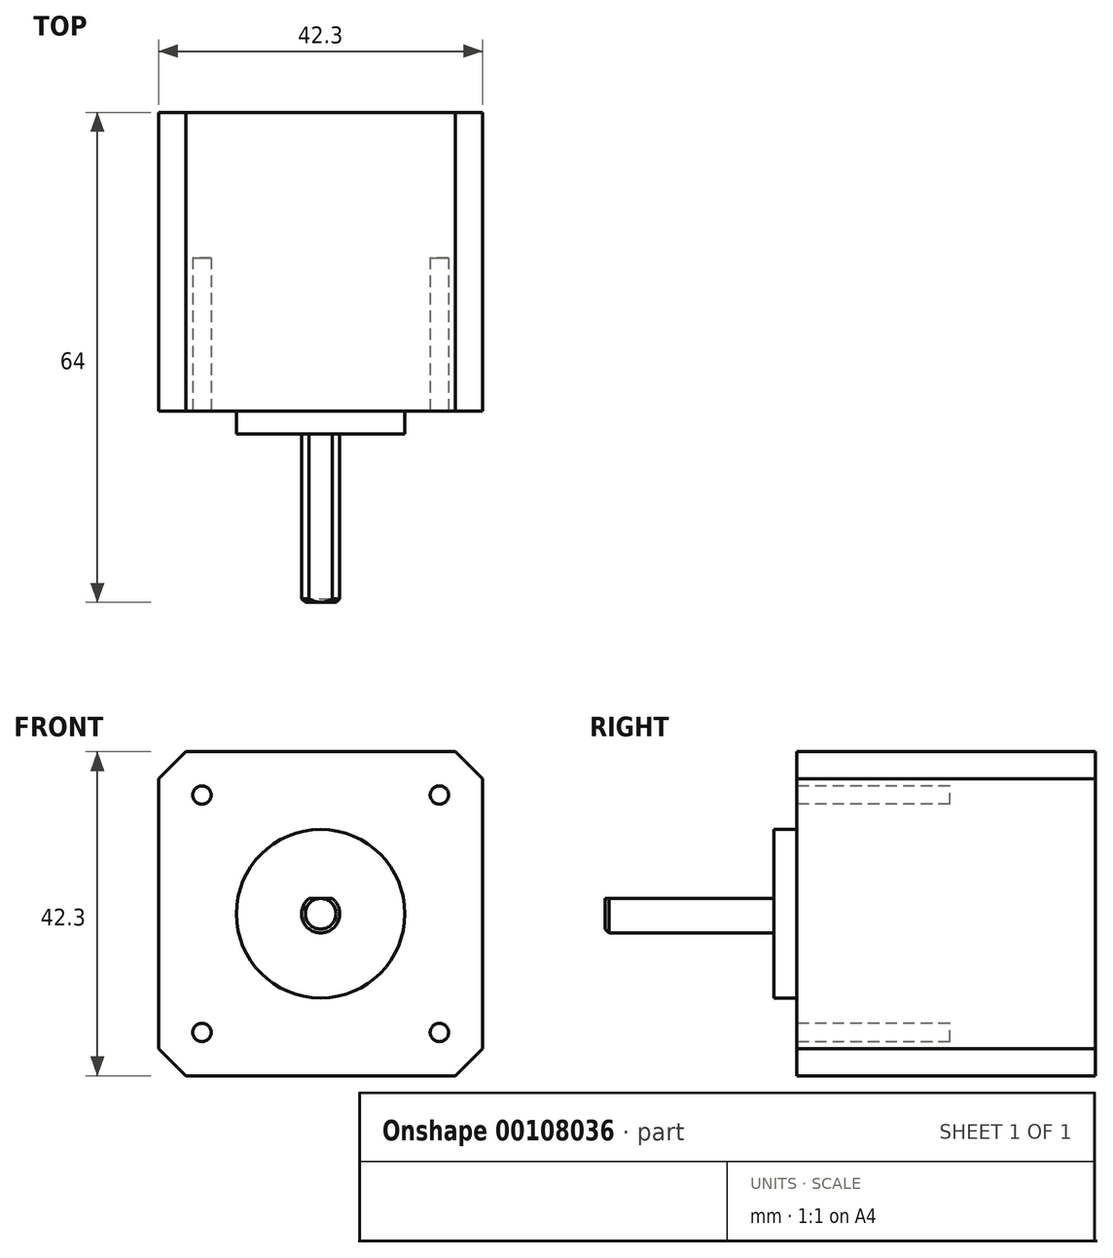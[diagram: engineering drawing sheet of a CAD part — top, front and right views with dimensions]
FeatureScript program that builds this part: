
annotation { "Feature Type Name" : "Feature", "Feature Type Description" : "" }
export const myFeature = defineFeature(function(context is Context, id is Id, definition is map)
    precondition{}
    {
        {
            var Q0;
            Q0=qCreatedBy(makeId("Front.planeOp"),FACE);
            var sketch = newSketch(context, id + "F0", { "sketchPlane" : qUnion([Q0])});
            skLineSegment(sketch, "E0.bottom", {"start": v(-17.61, 21.15) * mm, "end": v(17.61, 21.15) * mm});
            skLineSegment(sketch, "E0.top", {"start": v(-17.61, -21.15) * mm, "end": v(17.61, -21.15) * mm});
            skLineSegment(sketch, "E0.left", {"start": v(-21.15, 17.61) * mm, "end": v(-21.15, -17.61) * mm});
            skLineSegment(sketch, "E0.right", {"start": v(21.15, 17.61) * mm, "end": v(21.15, -17.61) * mm});
            skPoint(sketch, "E0.middle", {"position": v(0, 0) * mm});
            skLineSegment(sketch, "E1", {"start": v(-21.15, 17.61) * mm, "end": v(-17.61, 21.15) * mm});
            skLineSegment(sketch, "E2", {"start": v(0, 0) * mm, "end": v(0, 21.15) * mm, "construction": true});
            skLineSegment(sketch, "E3", {"start": v(0, 0) * mm, "end": v(21.15, 0) * mm, "construction": true});
            skLineSegment(sketch, "E4.MirrorCS", {"start": v(21.15, 17.61) * mm, "end": v(17.61, 21.15) * mm});
            skLineSegment(sketch, "E5.MirrorCS", {"start": v(-21.15, -17.61) * mm, "end": v(-17.61, -21.15) * mm});
            skLineSegment(sketch, "E6.MirrorCS", {"start": v(21.15, -17.61) * mm, "end": v(17.61, -21.15) * mm});
            skSolve(sketch);
        }
        {
            var Q0;
            Q0 = qSketchRegion(id + "F0", true);
            extrude(context, id + "F1", {"entities" : qUnion([Q0]), "endBound" : BoundingType.SYMMETRIC, "depth" : 39 * mm});
        }
        {
            var Q0;
            Q0=makeQuery(id+"F1.opExtrude","CAP_FACE",FACE,{"disambiguationData":[OSD([sQuery(id+"F0.wireOp",EDGE,"E0.bottom"),sQuery(id+"F0.wireOp",EDGE,"E0.top"),sQuery(id+"F0.wireOp",EDGE,"E0.left"),sQuery(id+"F0.wireOp",EDGE,"E0.right"),sQuery(id+"F0.wireOp",EDGE,"E1"),sQuery(id+"F0.wireOp",EDGE,"E4.MirrorCS"),sQuery(id+"F0.wireOp",EDGE,"E5.MirrorCS"),sQuery(id+"F0.wireOp",EDGE,"E6.MirrorCS")])],"isStart":false});
            var sketch = newSketch(context, id + "F2", { "sketchPlane" : qUnion([Q0])});
            skCircle(sketch, "E7", {"center": v(0, 0) * mm, "radius": 11 * mm});
            skSolve(sketch);
        }
        {
            var Q0;
            Q0 = qSketchRegion(id + "F2", true);
            extrude(context, id + "F3", {"entities" : qUnion([Q0]), "operationType" : NewBodyOperationType.ADD, "depth" : 3 * mm});
        }
        {
            var Q0;
            Q0=makeQuery(id+"F1.opExtrude","CAP_FACE",FACE,{"disambiguationData":[OSD([sQuery(id+"F0.wireOp",EDGE,"E0.bottom"),sQuery(id+"F0.wireOp",EDGE,"E0.top"),sQuery(id+"F0.wireOp",EDGE,"E0.left"),sQuery(id+"F0.wireOp",EDGE,"E0.right"),sQuery(id+"F0.wireOp",EDGE,"E1"),sQuery(id+"F0.wireOp",EDGE,"E4.MirrorCS"),sQuery(id+"F0.wireOp",EDGE,"E5.MirrorCS"),sQuery(id+"F0.wireOp",EDGE,"E6.MirrorCS")])],"isStart":false});
            var sketch = newSketch(context, id + "F4", { "sketchPlane" : qUnion([Q0])});
            skArc(sketch, "E8", {"start": v(-1.5, 2) * mm, "mid": v(0, -2.5) * mm, "end": v(1.5, 2) * mm});
            skLineSegment(sketch, "E9", {"start": v(-1.5, 2) * mm, "end": v(1.5, 2) * mm});
            skLineSegment(sketch, "E10", {"start": v(0, 2) * mm, "end": v(0, -2.5) * mm, "construction": true});
            skSolve(sketch);
        }
        {
            var Q0;
            Q0 = qSketchRegion(id + "F4", true);
            var Q1;
            Q1=makeQuery(id+"F1.opExtrude","CAP_FACE",FACE,{"disambiguationData":[OSD([sQuery(id+"F0.wireOp",EDGE,"E0.bottom"),sQuery(id+"F0.wireOp",EDGE,"E0.top"),sQuery(id+"F0.wireOp",EDGE,"E0.left"),sQuery(id+"F0.wireOp",EDGE,"E0.right"),sQuery(id+"F0.wireOp",EDGE,"E1"),sQuery(id+"F0.wireOp",EDGE,"E4.MirrorCS"),sQuery(id+"F0.wireOp",EDGE,"E5.MirrorCS"),sQuery(id+"F0.wireOp",EDGE,"E6.MirrorCS")])],"isStart":false});
            extrude(context, id + "F5", {"entities" : qUnion([Q0]), "operationType" : NewBodyOperationType.ADD, "depth" : 25 * mm});
        }
        {
            var Q0;
            Q0=makeQuery(id+"F5.opExtrude","CAP_EDGE",EDGE,{"disambiguationData":[OSD([sQuery(id+"F4.wireOp",EDGE,"E8")])],"isStart":false});
            chamfer(context, id + "F6", {"entities" : qUnion([Q0]), "width" : 0.5 * mm, "tangentPropagation" : true});
        }
        {
            var Q0;
            Q0=makeQuery(id+"F1.opExtrude","CAP_FACE",FACE,{"disambiguationData":[OSD([sQuery(id+"F0.wireOp",EDGE,"E0.bottom"),sQuery(id+"F0.wireOp",EDGE,"E0.top"),sQuery(id+"F0.wireOp",EDGE,"E0.left"),sQuery(id+"F0.wireOp",EDGE,"E0.right"),sQuery(id+"F0.wireOp",EDGE,"E1"),sQuery(id+"F0.wireOp",EDGE,"E4.MirrorCS"),sQuery(id+"F0.wireOp",EDGE,"E5.MirrorCS"),sQuery(id+"F0.wireOp",EDGE,"E6.MirrorCS")])],"isStart":false});
            var sketch = newSketch(context, id + "F7", { "sketchPlane" : qUnion([Q0])});
            skLineSegment(sketch, "E11.bottom", {"start": v(-15.5, 15.5) * mm, "end": v(15.5, 15.5) * mm, "construction": true});
            skLineSegment(sketch, "E11.top", {"start": v(-15.5, -15.5) * mm, "end": v(15.5, -15.5) * mm, "construction": true});
            skLineSegment(sketch, "E11.left", {"start": v(-15.5, 15.5) * mm, "end": v(-15.5, -15.5) * mm, "construction": true});
            skLineSegment(sketch, "E11.right", {"start": v(15.5, 15.5) * mm, "end": v(15.5, -15.5) * mm, "construction": true});
            skPoint(sketch, "E11.middle", {"position": v(0, 0) * mm});
            skCircle(sketch, "E12", {"center": v(-15.5, 15.5) * mm, "radius": 1.2 * mm});
            skCircle(sketch, "E13", {"center": v(15.5, 15.5) * mm, "radius": 1.2 * mm});
            skCircle(sketch, "E14", {"center": v(15.5, -15.5) * mm, "radius": 1.2 * mm});
            skCircle(sketch, "E15", {"center": v(-15.5, -15.5) * mm, "radius": 1.2 * mm});
            skSolve(sketch);
        }
        {
            var Q0;
            Q0 = qSketchRegion(id + "F7", true);
            extrude(context, id + "F8", {"entities" : qUnion([Q0]), "operationType" : NewBodyOperationType.REMOVE, "oppositeDirection" : true, "depth" : 20 * mm});
        }
    });
